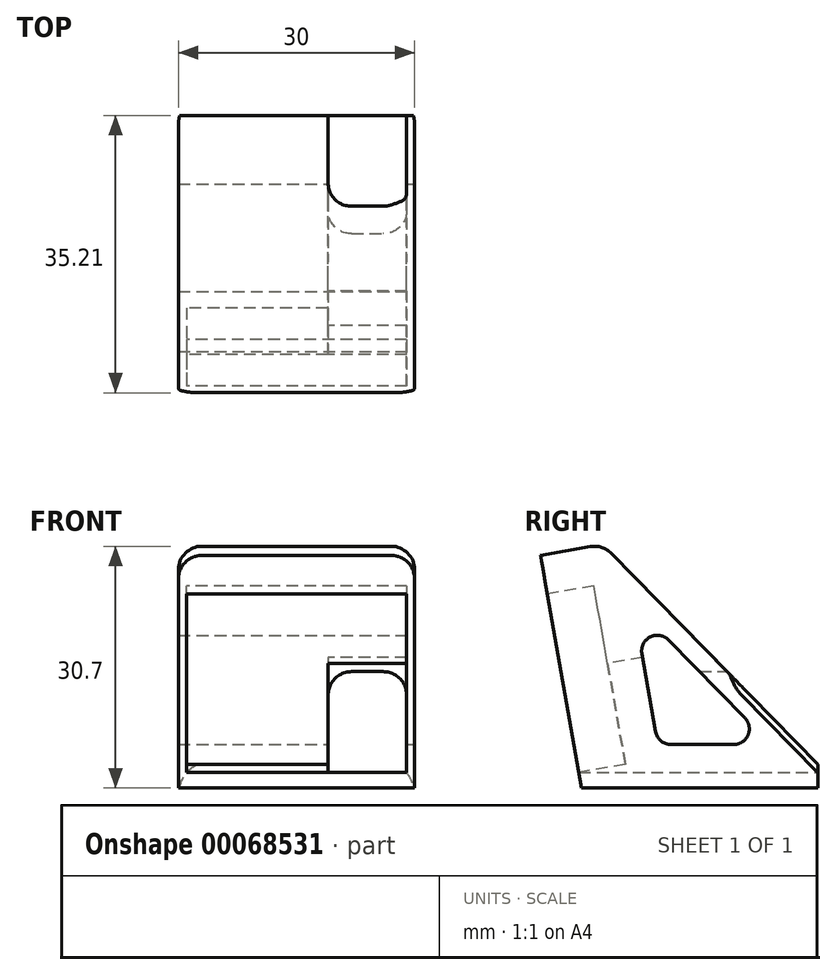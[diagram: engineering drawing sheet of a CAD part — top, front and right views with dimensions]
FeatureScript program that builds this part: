
annotation { "Feature Type Name" : "Feature", "Feature Type Description" : "" }
export const myFeature = defineFeature(function(context is Context, id is Id, definition is map)
    precondition{}
    {
        {
            var Q0;
            Q0=qCreatedBy(makeId("Top.planeOp"),FACE);
            var sketch = newSketch(context, id + "F0", { "sketchPlane" : qUnion([Q0])});
            skLineSegment(sketch, "E0.bottom", {"start": v(-15, 0) * mm, "end": v(15, 0) * mm});
            skLineSegment(sketch, "E0.top", {"start": v(-15, 30) * mm, "end": v(15, 30) * mm});
            skLineSegment(sketch, "E0.left", {"start": v(-15, 0) * mm, "end": v(-15, 30) * mm});
            skLineSegment(sketch, "E0.right", {"start": v(15, 0) * mm, "end": v(15, 30) * mm});
            skSolve(sketch);
        }
        {
            var Q0;
            Q0=qCreatedBy(makeId("Right.planeOp"),FACE);
            var sketch = newSketch(context, id + "F1", { "sketchPlane" : qUnion([Q0])});
            skPoint(sketch, "E1.0", {"position": v(0, 0) * mm});
            skLineSegment(sketch, "E2.0", {"start": v(0, 0) * mm, "end": v(30, 0) * mm});
            skLineSegment(sketch, "E3", {"start": v(0, 0) * mm, "end": v(-3.47, 19.7) * mm});
            skSolve(sketch);
        }
        {
            var Q0;
            Q0=sQuery(id+"F0.wireOp",VERTEX,"E0.right.start");
            var Q1;
            Q1=sQuery(id+"F1.wireOp",VERTEX,"E3.end");
            var Q2;
            Q2=sQuery(id+"F0.wireOp",VERTEX,"E0.left.start");
            cPlane(context, id + "F2", {"entities" : qUnion([Q0, Q1, Q2]), "cplaneType" : CPlaneType.THREE_POINT, "offset" : 150 * mm, "width" : 150 * mm, "height" : 150 * mm});
        }
        {
            var Q0;
            Q0=qCreatedBy(id+"F2.planeOp",FACE);
            var sketch = newSketch(context, id + "F3", { "sketchPlane" : qUnion([Q0])});
            skPoint(sketch, "E4.0", {"position": v(15, 0) * mm});
            skPoint(sketch, "E5.0", {"position": v(-15, 0) * mm});
            skPoint(sketch, "E6.0", {"position": v(0, 20) * mm});
            skLineSegment(sketch, "E7", {"start": v(-9, 8.5) * mm, "end": v(-7.56, 0) * mm, "construction": true});
            skPoint(sketch, "E7.startSnap0", {"position": v(-9, 5.5) * mm});
            skLineSegment(sketch, "E8.rect.bottom", {"start": v(-14, 15) * mm, "end": v(-4, 15) * mm});
            skLineSegment(sketch, "E8.rect.top", {"start": v(-14, 2) * mm, "end": v(-4, 2) * mm});
            skLineSegment(sketch, "E8.rect.left", {"start": v(-14, 15) * mm, "end": v(-14, 2) * mm});
            skLineSegment(sketch, "E8.rect.right", {"start": v(-4, 15) * mm, "end": v(-4, 2) * mm});
            skPoint(sketch, "E8.rect.middle", {"position": v(-9, 8.5) * mm});
            skPoint(sketch, "E9.rect.middle", {"position": v(0, 10.02) * mm});
            skLineSegment(sketch, "E10.bottom", {"start": v(15, 0) * mm, "end": v(-15, 0) * mm});
            skLineSegment(sketch, "E10.top", {"start": v(15, 30) * mm, "end": v(-15, 30) * mm});
            skLineSegment(sketch, "E10.left", {"start": v(15, 0) * mm, "end": v(15, 30) * mm});
            skLineSegment(sketch, "E10.right", {"start": v(-15, 0) * mm, "end": v(-15, 30) * mm});
            skPoint(sketch, "E11", {"position": v(0, 15) * mm});
            skPoint(sketch, "E11.positionSnap0", {"position": v(-15, 15) * mm});
            skPoint(sketch, "E12", {"position": v(0, 17.5) * mm});
            skLineSegment(sketch, "E13.rect.bottom", {"start": v(-14, 2) * mm, "end": v(14, 2) * mm});
            skLineSegment(sketch, "E13.rect.top", {"start": v(-14, 25) * mm, "end": v(14, 25) * mm});
            skLineSegment(sketch, "E13.rect.left", {"start": v(-14, 2) * mm, "end": v(-14, 25) * mm});
            skLineSegment(sketch, "E13.rect.right", {"start": v(14, 2) * mm, "end": v(14, 25) * mm});
            skSolve(sketch);
        }
        {
            var Q0;
            Q0=makeQuery(id+"F0.imprint","IMPRINT",FACE,{"disambiguationData":[TD([[makeQuery(id+"F0.imprint","IMPRINT",EDGE,{"derivedFrom":sQuery(id+"F0.wireOp",EDGE,"E0.bottom")}),1.0]])]});
            extrude(context, id + "F4", {"entities" : qUnion([Q0]), "depth" : 3 * mm});
        }
        {
            var Q0;
            Q0=makeQuery(id+"F3.imprint","IMPRINT",FACE,{"disambiguationData":[TD([[makeQuery(id+"F3.imprint","IMPRINT",EDGE,{"derivedFrom":sQuery(id+"F3.wireOp",EDGE,"E10.bottom")}),-1.0]])]});
            var Q1;
            Q1=makeQuery(id+"F3.imprint","IMPRINT",FACE,{"disambiguationData":[TD([[makeQuery(id+"F3.imprint","IMPRINT",EDGE,{"derivedFrom":sQuery(id+"F3.wireOp",EDGE,"E8.rect.bottom")}),1.0]])]});
            extrude(context, id + "F5", {"entities" : qUnion([Q0, Q1]), "operationType" : NewBodyOperationType.ADD, "depth" : 8 * mm});
        }
        {
            var Q0;
            Q0=makeQuery(id+"F0.imprint","IMPRINT",FACE,{"disambiguationData":[TD([[makeQuery(id+"F0.imprint","IMPRINT",EDGE,{"derivedFrom":sQuery(id+"F0.wireOp",EDGE,"E0.bottom")}),1.0]])]});
            extrude(context, id + "F6", {"entities" : qUnion([Q0]), "operationType" : NewBodyOperationType.REMOVE, "oppositeDirection" : true, "depth" : 25 * mm});
        }
        {
            var Q0;
            Q0=makeQuery(id+"F4.opExtrude","SWEPT_FACE",FACE,{"disambiguationData":[OSD([sQuery(id+"F0.wireOp",EDGE,"E0.top")])]});
            var sketch = newSketch(context, id + "F7", { "sketchPlane" : qUnion([Q0])});
            skLineSegment(sketch, "E14.0", {"start": v(-4, 14.77) * mm, "end": v(-4, 1.97) * mm});
            skLineSegment(sketch, "E15.0", {"start": v(-14, 1.97) * mm, "end": v(-4, 1.97) * mm});
            skLineSegment(sketch, "E16.0", {"start": v(-14, 14.77) * mm, "end": v(-14, 1.97) * mm});
            skLineSegment(sketch, "E17.0", {"start": v(-14, 14.77) * mm, "end": v(-4, 14.77) * mm});
            skSolve(sketch);
        }
        {
            var Q0;
            Q0=makeQuery(id+"F3.imprint","IMPRINT",FACE,{"disambiguationData":[TD([[makeQuery(id+"F3.imprint","IMPRINT",EDGE,{"derivedFrom":sQuery(id+"F3.wireOp",EDGE,"E8.rect.bottom")}),1.0]])]});
            extrude(context, id + "F8", {"entities" : qUnion([Q0]), "operationType" : NewBodyOperationType.REMOVE, "depth" : 6 * mm});
        }
        {
            var Q0;
            Q0=makeQuery(id+"F5.boolean.opBoolean","MERGE",FACE,{"derivedFrom":[makeQuery(id+"F4.opExtrude","SWEPT_FACE",FACE,{"disambiguationData":[OSD([sQuery(id+"F0.wireOp",EDGE,"E0.right")])]}),makeQuery(id+"F5.opExtrude","SWEPT_FACE",FACE,{"disambiguationData":[OSD([sQuery(id+"F3.wireOp",EDGE,"E10.right")])]})]});
            var sketch = newSketch(context, id + "F9", { "sketchPlane" : qUnion([Q0])});
            skPoint(sketch, "E18.0", {"position": v(30, 3) * mm});
            skPoint(sketch, "E19.0", {"position": v(2.67, 30.93) * mm});
            skLineSegment(sketch, "E20", {"start": v(2.67, 30.93) * mm, "end": v(30, 3) * mm});
            skPoint(sketch, "E21.0", {"position": v(7.6, 3) * mm});
            skLineSegment(sketch, "E22", {"start": v(7.6, 3) * mm, "end": v(2.67, 30.93) * mm});
            skLineSegment(sketch, "E23", {"start": v(7.6, 3) * mm, "end": v(30, 3) * mm});
            skLineSegment(sketch, "E24.0", {"start": v(9.4, 7.15) * mm, "end": v(7.66, 17.04) * mm});
            skLineSegment(sketch, "E24.1", {"start": v(11.37, 5.5) * mm, "end": v(19.3, 5.5) * mm});
            skLineSegment(sketch, "E24.2", {"start": v(11.06, 18.79) * mm, "end": v(20.73, 8.9) * mm});
            skPoint(sketch, "E25.visualSharp", {"position": v(6.53, 23.4) * mm});
            skArc(sketch, "E25.filletArc", {"start": v(11.06, 18.79) * mm, "mid": v(8.71, 19.17) * mm, "end": v(7.66, 17.04) * mm});
            skPoint(sketch, "E26.visualSharp", {"position": v(9.7, 5.5) * mm});
            skArc(sketch, "E26.filletArc", {"start": v(9.4, 7.15) * mm, "mid": v(10.08, 5.97) * mm, "end": v(11.37, 5.5) * mm});
            skPoint(sketch, "E27.visualSharp", {"position": v(24.06, 5.5) * mm});
            skArc(sketch, "E27.filletArc", {"start": v(19.3, 5.5) * mm, "mid": v(21.14, 6.72) * mm, "end": v(20.73, 8.9) * mm});
            skSolve(sketch);
        }
        {
            var Q0;
            Q0=makeQuery(id+"F9.imprint","IMPRINT",FACE,{"disambiguationData":[TD([[makeQuery(id+"F9.imprint","IMPRINT",EDGE,{"derivedFrom":sQuery(id+"F9.wireOp",EDGE,"E20")}),-1.0]])]});
            var Q1;
            Q1=makeQuery(id+"F5.boolean.opBoolean","MERGE",FACE,{"derivedFrom":[makeQuery(id+"F4.opExtrude","SWEPT_FACE",FACE,{"disambiguationData":[OSD([sQuery(id+"F0.wireOp",EDGE,"E0.left")])]}),makeQuery(id+"F5.opExtrude","SWEPT_FACE",FACE,{"disambiguationData":[OSD([sQuery(id+"F3.wireOp",EDGE,"E10.left")])]})]});
            extrude(context, id + "F10", {"entities" : qUnion([Q0]), "operationType" : NewBodyOperationType.ADD, "endBound" : BoundingType.UP_TO_SURFACE, "oppositeDirection" : true, "endBoundEntityFace" : qUnion([Q1]), "depth" : 25 * mm});
        }
        {
            var Q0;
            {var subQ0=sQuery(id+"F7.wireOp",EDGE,"E17.0");Q0=makeQuery(id+"F7.imprint","IMPRINT",FACE,{"disambiguationData":[TD([[makeQuery(id+"F7.imprint","IMPRINT",EDGE,{"derivedFrom":subQ0}),-1.0]])]});}
            var Q1;
            {var subQ0=sQuery(id+"F7.wireOp",EDGE,"E15.0");Q1=makeQuery(id+"F7.imprint","IMPRINT",FACE,{"disambiguationData":[TD([[makeQuery(id+"F7.imprint","IMPRINT",EDGE,{"derivedFrom":subQ0}),1.0]])]});}
            extrude(context, id + "F11", {"entities" : qUnion([Q0, Q1]), "operationType" : NewBodyOperationType.REMOVE, "endBound" : BoundingType.THROUGH_ALL, "oppositeDirection" : true, "depth" : 100 * mm});
        }
        {
            var Q0;
            Q0=makeQuery(id+"F5.opExtrude","SWEPT_EDGE",EDGE,{"disambiguationData":[OSD([sQuery(id+"F3.wireOp",EDGE,"E10.top"),sQuery(id+"F3.wireOp",EDGE,"E10.left")])]});
            var Q1;
            Q1=makeQuery(id+"F5.opExtrude","SWEPT_EDGE",EDGE,{"disambiguationData":[OSD([sQuery(id+"F3.wireOp",EDGE,"E10.top"),sQuery(id+"F3.wireOp",EDGE,"E10.right")])]});
            var Q2;
            {var subQ0=sQuery(id+"F3.wireOp",EDGE,"E10.top");Q2=makeQuery(id+"F10.boolean.opBoolean","MERGE",EDGE,{"derivedFrom":[makeQuery(id+"F5.opExtrude","CAP_EDGE",EDGE,{"disambiguationData":[OSD([subQ0])],"isStart":false}),makeQuery(id+"F10.opExtrude","SWEPT_EDGE",EDGE,{"disambiguationData":[OSD([subQ0,sQuery(id+"F3.wireOp",EDGE,"E10.right"),sQuery(id+"F9.wireOp",EDGE,"E20"),sQuery(id+"F9.wireOp",EDGE,"E22")])]})]});}
            var Q3;
            Q3=makeQuery(id+"F10.opExtrude","CAP_EDGE",EDGE,{"disambiguationData":[OSD([sQuery(id+"F9.wireOp",EDGE,"E20")])],"isStart":false});
            var Q4;
            Q4=makeQuery(id+"F10.opExtrude","CAP_EDGE",EDGE,{"disambiguationData":[OSD([sQuery(id+"F9.wireOp",EDGE,"E20")])],"isStart":true});
            var Q5;
            Q5=makeQuery(id+"F11.boolean.opBoolean","COPY",EDGE,{"disambiguationData":[OD(1.0)],"derivedFrom":makeQuery(id+"F11.opExtrude","SWEPT_EDGE",EDGE,{"disambiguationData":[OSD([sQuery(id+"F7.wireOp",EDGE,"E14.0"),sQuery(id+"F7.wireOp",EDGE,"E17.0")])]})});
            var Q6;
            Q6=makeQuery(id+"F11.boolean.opBoolean","COPY",EDGE,{"disambiguationData":[OD(1.0)],"derivedFrom":makeQuery(id+"F11.opExtrude","SWEPT_EDGE",EDGE,{"disambiguationData":[OSD([sQuery(id+"F7.wireOp",EDGE,"E16.0"),sQuery(id+"F7.wireOp",EDGE,"E17.0")])]})});
            fillet(context, id + "F12", {"entities" : qUnion([Q0, Q1, Q2, Q3, Q4, Q5, Q6]), "radius" : 3 * mm, "tangentPropagation" : true, "allowEdgeOverflow" : false});
        }
        {
            var Q0;
            Q0=makeQuery(id+"F3.imprint","IMPRINT",FACE,{"disambiguationData":[TD([[makeQuery(id+"F3.imprint","IMPRINT",EDGE,{"derivedFrom":sQuery(id+"F3.wireOp",EDGE,"E10.bottom")}),-1.0]])]});
            var Q1;
            Q1=makeQuery(id+"F3.imprint","IMPRINT",FACE,{"disambiguationData":[TD([[makeQuery(id+"F3.imprint","IMPRINT",EDGE,{"derivedFrom":sQuery(id+"F3.wireOp",EDGE,"E8.rect.bottom")}),1.0]])]});
            var Q2;
            Q2=makeQuery(id+"F3.imprint","IMPRINT",FACE,{"disambiguationData":[TD([[makeQuery(id+"F3.imprint","IMPRINT",EDGE,{"derivedFrom":sQuery(id+"F3.wireOp",EDGE,"E8.rect.bottom")}),-1.0]])]});
            extrude(context, id + "F13", {"entities" : qUnion([Q0, Q1, Q2]), "operationType" : NewBodyOperationType.REMOVE, "endBound" : BoundingType.THROUGH_ALL, "oppositeDirection" : true, "depth" : 25 * mm});
        }
        {
            var Q0;
            Q0=makeQuery(id+"F3.imprint","IMPRINT",FACE,{"disambiguationData":[TD([[makeQuery(id+"F3.imprint","IMPRINT",EDGE,{"derivedFrom":sQuery(id+"F3.wireOp",EDGE,"E8.rect.bottom")}),-1.0]])]});
            var Q1;
            Q1=makeQuery(id+"F10.opExtrude","SWEPT_FACE",FACE,{"disambiguationData":[OSD([sQuery(id+"F9.wireOp",EDGE,"E24.0")])]});
            extrude(context, id + "F14", {"entities" : qUnion([Q0]), "operationType" : NewBodyOperationType.REMOVE, "endBound" : BoundingType.UP_TO_SURFACE, "endBoundEntityFace" : qUnion([Q1]), "depth" : 25 * mm});
        }
    });
